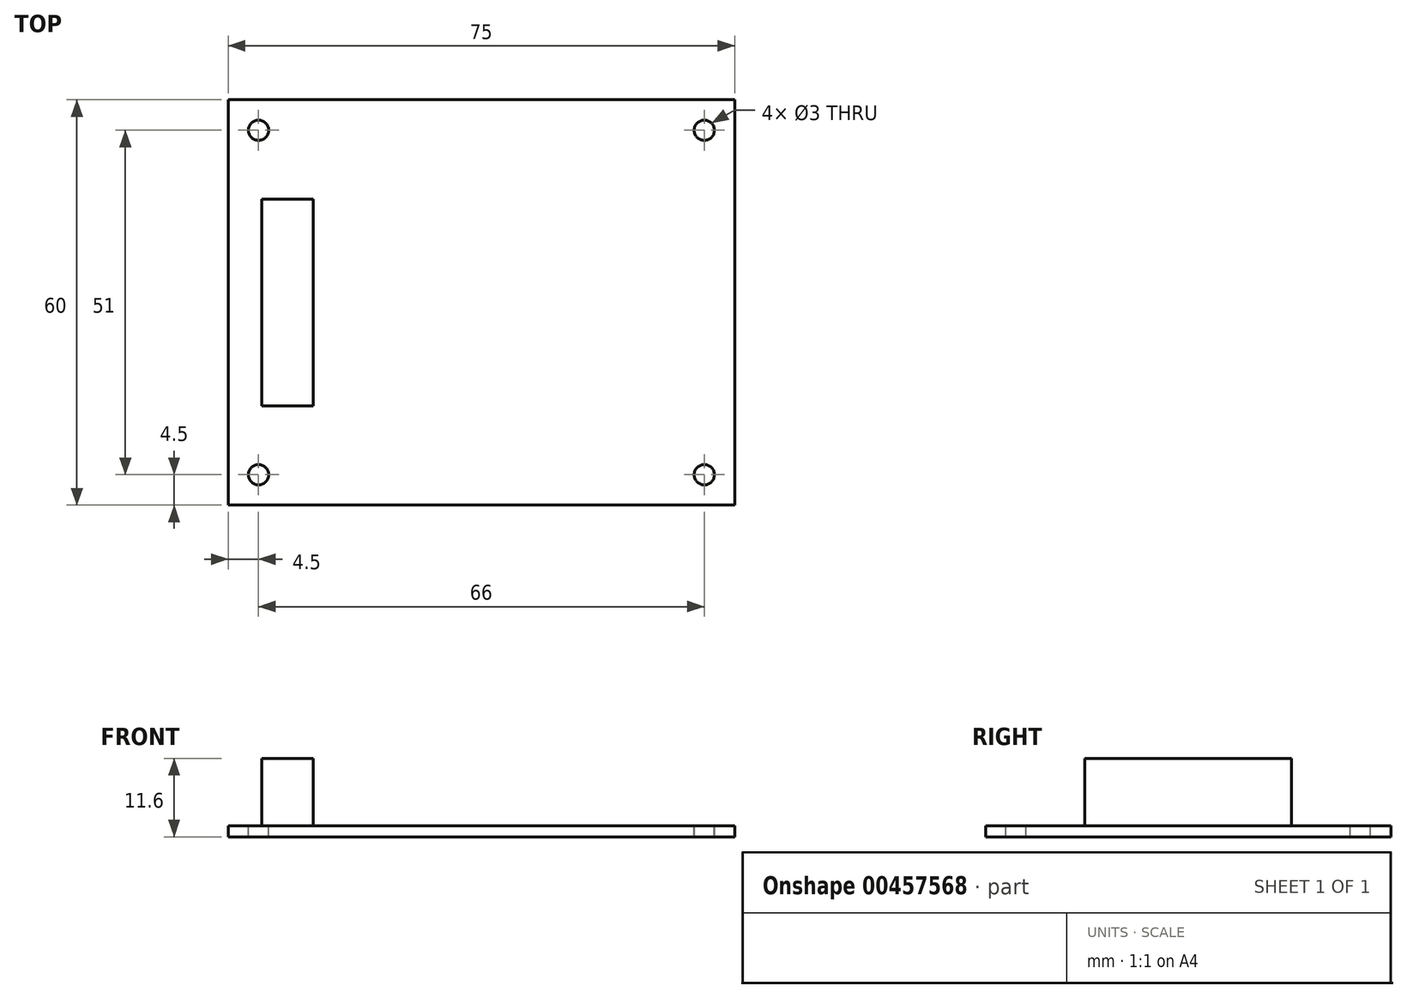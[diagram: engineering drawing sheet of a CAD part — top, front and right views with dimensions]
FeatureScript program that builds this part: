
annotation { "Feature Type Name" : "Feature", "Feature Type Description" : "" }
export const myFeature = defineFeature(function(context is Context, id is Id, definition is map)
    precondition{}
    {
        {
            var Q0;
            Q0=qCreatedBy(makeId("Top.planeOp"),FACE);
            var sketch = newSketch(context, id + "F0", { "sketchPlane" : qUnion([Q0])});
            skLineSegment(sketch, "E0.bottom", {"start": v(-37.5, 30) * mm, "end": v(37.5, 30) * mm});
            skLineSegment(sketch, "E0.top", {"start": v(-37.5, -30) * mm, "end": v(37.5, -30) * mm});
            skLineSegment(sketch, "E0.left", {"start": v(-37.5, 30) * mm, "end": v(-37.5, -30) * mm});
            skLineSegment(sketch, "E0.right", {"start": v(37.5, 30) * mm, "end": v(37.5, -30) * mm});
            skPoint(sketch, "E0.middle", {"position": v(0, 0) * mm});
            skSolve(sketch);
        }
        {
            var Q0;
            Q0 = qSketchRegion(id + "F0", true);
            extrude(context, id + "F1", {"entities" : qUnion([Q0]), "depth" : 1.6 * mm});
        }
        {
            var Q0;
            Q0=makeQuery(id+"F1.opExtrude","CAP_FACE",FACE,{"disambiguationData":[OSD([sQuery(id+"F0.wireOp",EDGE,"E0.bottom"),sQuery(id+"F0.wireOp",EDGE,"E0.top"),sQuery(id+"F0.wireOp",EDGE,"E0.left"),sQuery(id+"F0.wireOp",EDGE,"E0.right")])],"isStart":false});
            var sketch = newSketch(context, id + "F2", { "sketchPlane" : qUnion([Q0])});
            skLineSegment(sketch, "E1.bottom", {"start": v(-32.5, 15.3) * mm, "end": v(-24.9, 15.3) * mm});
            skLineSegment(sketch, "E1.top", {"start": v(-32.5, -15.3) * mm, "end": v(-24.9, -15.3) * mm});
            skLineSegment(sketch, "E1.left", {"start": v(-32.5, 15.3) * mm, "end": v(-32.5, -15.3) * mm});
            skLineSegment(sketch, "E1.right", {"start": v(-24.9, 15.3) * mm, "end": v(-24.9, -15.3) * mm});
            skSolve(sketch);
        }
        {
            var Q0;
            Q0 = qSketchRegion(id + "F2", true);
            extrude(context, id + "F3", {"entities" : qUnion([Q0]), "operationType" : NewBodyOperationType.ADD, "depth" : 10 * mm});
        }
        {
            var Q0;
            Q0=makeQuery(id+"F1.opExtrude","CAP_FACE",FACE,{"disambiguationData":[OSD([sQuery(id+"F0.wireOp",EDGE,"E0.bottom"),sQuery(id+"F0.wireOp",EDGE,"E0.top"),sQuery(id+"F0.wireOp",EDGE,"E0.left"),sQuery(id+"F0.wireOp",EDGE,"E0.right")])],"isStart":false});
            var sketch = newSketch(context, id + "F4", { "sketchPlane" : qUnion([Q0])});
            skCircle(sketch, "E2", {"center": v(-33, 25.5) * mm, "radius": 1.5 * mm});
            skSolve(sketch);
        }
        {
            var Q0;
            Q0=sQuery(id+"F4.wireOp",VERTEX,"E2.center");
            var Q1;
            Q1=makeQuery(id+"F1.opExtrude","SWEPT_BODY",BODY,{"disambiguationData":[OSD([sQuery(id+"F0.wireOp",EDGE,"E0.bottom"),sQuery(id+"F0.wireOp",EDGE,"E0.top"),sQuery(id+"F0.wireOp",EDGE,"E0.left"),sQuery(id+"F0.wireOp",EDGE,"E0.right")])]});
            hole(context, id + "F5", {"style" : HoleStyle.SIMPLE, "endStyle" : HoleEndStyle.THROUGH, "holeDiameter" : 3 * mm, "isTappedThrough" : true, "tappedDepth" : 12 * mm, "tapClearance" : 3, "locations" : qUnion([Q0]), "scope" : qUnion([Q1])});
        }
        {
            var Q0;
            Q0=qCreatedBy(makeId("Top.planeOp"),FACE);
            var sketch = newSketch(context, id + "F6", { "sketchPlane" : qUnion([Q0])});
            skCircle(sketch, "E3", {"center": v(33, 25.5) * mm, "radius": 1.5 * mm});
            skSolve(sketch);
        }
        {
            var Q0;
            Q0=sQuery(id+"F6.wireOp",VERTEX,"E3.center");
            var Q1;
            Q1=makeQuery(id+"F1.opExtrude","SWEPT_BODY",BODY,{"disambiguationData":[OSD([sQuery(id+"F0.wireOp",EDGE,"E0.bottom"),sQuery(id+"F0.wireOp",EDGE,"E0.top"),sQuery(id+"F0.wireOp",EDGE,"E0.left"),sQuery(id+"F0.wireOp",EDGE,"E0.right")])]});
            hole(context, id + "F7", {"style" : HoleStyle.SIMPLE, "endStyle" : HoleEndStyle.THROUGH, "oppositeDirection" : true, "holeDiameter" : 3 * mm, "isTappedThrough" : true, "tappedDepth" : 12 * mm, "tapClearance" : 3, "locations" : qUnion([Q0]), "scope" : qUnion([Q1])});
        }
        {
            var Q0;
            Q0=makeQuery(id+"F1.opExtrude","CAP_FACE",FACE,{"disambiguationData":[OSD([sQuery(id+"F0.wireOp",EDGE,"E0.bottom"),sQuery(id+"F0.wireOp",EDGE,"E0.top"),sQuery(id+"F0.wireOp",EDGE,"E0.left"),sQuery(id+"F0.wireOp",EDGE,"E0.right")])],"isStart":false});
            var sketch = newSketch(context, id + "F8", { "sketchPlane" : qUnion([Q0])});
            skCircle(sketch, "E4", {"center": v(33, -25.5) * mm, "radius": 1.5 * mm});
            skSolve(sketch);
        }
        {
            var Q0;
            Q0=sQuery(id+"F8.wireOp",VERTEX,"E4.center");
            var Q1;
            Q1=makeQuery(id+"F1.opExtrude","SWEPT_BODY",BODY,{"disambiguationData":[OSD([sQuery(id+"F0.wireOp",EDGE,"E0.bottom"),sQuery(id+"F0.wireOp",EDGE,"E0.top"),sQuery(id+"F0.wireOp",EDGE,"E0.left"),sQuery(id+"F0.wireOp",EDGE,"E0.right")])]});
            hole(context, id + "F9", {"style" : HoleStyle.SIMPLE, "endStyle" : HoleEndStyle.THROUGH, "holeDiameter" : 3 * mm, "isTappedThrough" : true, "tappedDepth" : 12 * mm, "tapClearance" : 3, "locations" : qUnion([Q0]), "scope" : qUnion([Q1])});
        }
        {
            var Q0;
            Q0=makeQuery(id+"F1.opExtrude","CAP_FACE",FACE,{"disambiguationData":[OSD([sQuery(id+"F0.wireOp",EDGE,"E0.bottom"),sQuery(id+"F0.wireOp",EDGE,"E0.top"),sQuery(id+"F0.wireOp",EDGE,"E0.left"),sQuery(id+"F0.wireOp",EDGE,"E0.right")])],"isStart":false});
            var sketch = newSketch(context, id + "F10", { "sketchPlane" : qUnion([Q0])});
            skCircle(sketch, "E5", {"center": v(-33, -25.5) * mm, "radius": 1.5 * mm});
            skSolve(sketch);
        }
        {
            var Q0;
            Q0=sQuery(id+"F10.wireOp",VERTEX,"E5.center");
            var Q1;
            Q1=makeQuery(id+"F1.opExtrude","SWEPT_BODY",BODY,{"disambiguationData":[OSD([sQuery(id+"F0.wireOp",EDGE,"E0.bottom"),sQuery(id+"F0.wireOp",EDGE,"E0.top"),sQuery(id+"F0.wireOp",EDGE,"E0.left"),sQuery(id+"F0.wireOp",EDGE,"E0.right")])]});
            hole(context, id + "F11", {"style" : HoleStyle.SIMPLE, "endStyle" : HoleEndStyle.THROUGH, "holeDiameter" : 3 * mm, "isTappedThrough" : true, "tappedDepth" : 12 * mm, "tapClearance" : 3, "locations" : qUnion([Q0]), "scope" : qUnion([Q1])});
        }
        {
            var Q0;
            Q0=makeQuery(id+"F1.opExtrude","SWEPT_BODY",BODY,{"disambiguationData":[OSD([sQuery(id+"F0.wireOp",EDGE,"E0.bottom"),sQuery(id+"F0.wireOp",EDGE,"E0.top"),sQuery(id+"F0.wireOp",EDGE,"E0.left"),sQuery(id+"F0.wireOp",EDGE,"E0.right")])]});
            transform(context, id + "F12", {"entities" : qUnion([Q0]), "transformType" : TransformType.TRANSLATION_3D, "dx" : 0 * mm, "dy" : 0 * mm, "dz" : 0 * mm, "makeCopy" : true});
        }
        {
            var Q0;
            Q0=makeQuery(id+"F12.opPattern","COPY",BODY,{"derivedFrom":makeQuery(id+"F1.opExtrude","SWEPT_BODY",BODY,{"disambiguationData":[OSD([sQuery(id+"F0.wireOp",EDGE,"E0.bottom"),sQuery(id+"F0.wireOp",EDGE,"E0.top"),sQuery(id+"F0.wireOp",EDGE,"E0.left"),sQuery(id+"F0.wireOp",EDGE,"E0.right")])]}),"instanceName":"1"});
            deleteBodies(context, id + "F13", {"entities" : qUnion([Q0])});
        }
    });
